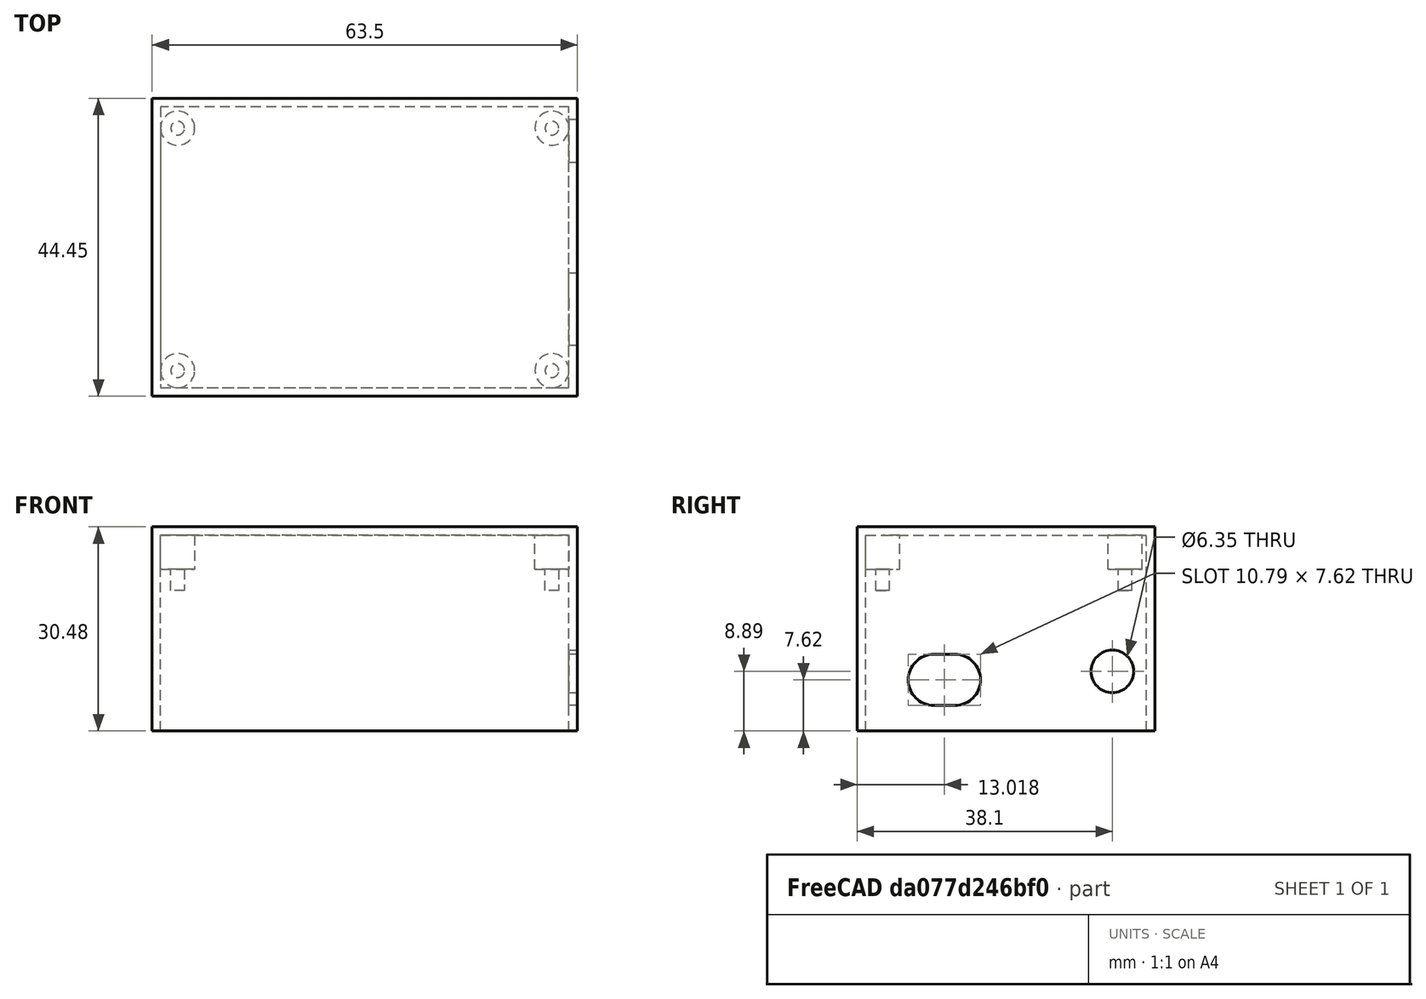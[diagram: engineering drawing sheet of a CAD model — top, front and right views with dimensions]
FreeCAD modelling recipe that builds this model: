
FCSTD DOCUMENT  (FreeCAD 0.18R4 (GitTag))
Label: BluetoothLightControlBox
License: All rights reserved
LicenseURL: http://en.wikipedia.org/wiki/All_rights_reserved
objects: Sketcher::SketchObject×5, PartDesign::Pad×3, PartDesign::Pocket×2, PartDesign::Body×1
note: 16 computed .brp shape members not serialized (recipe doc carries the construction recipe); baked Part::Feature solids carry a one-line shape summary decoded from their .brp

FEATURE [Sketcher::SketchObject] Sketch
  MapMode = 5
  Support = -> [XY_Plane]
  sketch-geometry (4):
    g0: LineSegment StartX=0 StartY=0 StartZ=0 EndX=63.5 EndY=0 EndZ=0
    g1: LineSegment StartX=63.5 StartY=0 StartZ=0 EndX=63.5 EndY=44.45 EndZ=0
    g2: LineSegment StartX=63.5 StartY=44.45 StartZ=0 EndX=0 EndY=44.45 EndZ=0
    g3: LineSegment StartX=0 StartY=44.45 StartZ=0 EndX=0 EndY=0 EndZ=0
  constraints (11):
    c: Coincident(g0,g1)
    c: Coincident(g1,g2)
    c: Coincident(g2,g3)
    c: Coincident(g3,g0)
    c: Horizontal(g0)
    c: Horizontal(g2)
    c: Vertical(g1)
    c: Vertical(g3)
    c: Coincident(g0,g-1)
    c: DistanceX(g2,g2) = 63.5
    c: DistanceY(g1,g1) = 44.45
FEATURE [PartDesign::Pad] Pad
  Length = 30.48
  Length2 = 100.076
  Profile = -> Sketch
  Type = 0
FEATURE [Sketcher::SketchObject] Sketch001
  MapMode = 5
  Placement = pos=(0,0,0) rot=(1,0,0;3.14159rad)
  Support = -> [Pad]
  sketch-geometry (4):
    g0: LineSegment StartX=1.27 StartY=-1.27 StartZ=0 EndX=62.23 EndY=-1.27 EndZ=0
    g1: LineSegment StartX=62.23 StartY=-1.27 StartZ=0 EndX=62.23 EndY=-43.18 EndZ=0
    g2: LineSegment StartX=62.23 StartY=-43.18 StartZ=0 EndX=1.27 EndY=-43.18 EndZ=0
    g3: LineSegment StartX=1.27 StartY=-43.18 StartZ=0 EndX=1.27 EndY=-1.27 EndZ=0
  constraints (12):
    c: Coincident(g0,g1)
    c: Coincident(g1,g2)
    c: Coincident(g2,g3)
    c: Coincident(g3,g0)
    c: Horizontal(g0)
    c: Horizontal(g2)
    c: Vertical(g1)
    c: Vertical(g3)
    c: DistanceY(g1,g1) = 41.91
    c: DistanceX(g0,g0) = 60.96
    c: DistanceX(g-1,g0) = 1.27
    c: DistanceY(g0,g-1) = 1.27
FEATURE [PartDesign::Pocket] Pocket
  BaseFeature = -> Pad
  Length = 29.21
  Length2 = 100.076
  Profile = -> Sketch001
  Type = 0
FEATURE [Sketcher::SketchObject] Sketch002
  MapMode = 5
  Placement = pos=(0,0,29.21) rot=(1,0,0;3.14159rad)
  Support = -> [Pocket]
  sketch-geometry (8):
    g0: Circle CenterX=3.81 CenterY=-40.005 CenterZ=0 NormalX=0 NormalY=0 NormalZ=1 AngleXU=0 Radius=2.54
    g1: Circle CenterX=59.69 CenterY=-40.005 CenterZ=0 NormalX=0 NormalY=0 NormalZ=1 AngleXU=0 Radius=2.54
    g2: Circle CenterX=3.81 CenterY=-3.81 CenterZ=0 NormalX=0 NormalY=0 NormalZ=1 AngleXU=0 Radius=2.54
    g3: Circle CenterX=59.69 CenterY=-3.81 CenterZ=0 NormalX=0 NormalY=0 NormalZ=1 AngleXU=0 Radius=2.54
    g4: LineSegment [constr] StartX=3.81 StartY=-3.81 StartZ=0 EndX=59.69 EndY=-3.81 EndZ=0
    g5: LineSegment [constr] StartX=59.69 StartY=-3.81 StartZ=0 EndX=59.69 EndY=-40.005 EndZ=0
    g6: LineSegment [constr] StartX=59.69 StartY=-40.005 StartZ=0 EndX=3.81 EndY=-40.005 EndZ=0
    g7: LineSegment [constr] StartX=3.81 StartY=-40.005 StartZ=0 EndX=3.81 EndY=-3.81 EndZ=0
  constraints (20):
    c: Coincident(g4,g5)
    c: Coincident(g5,g6)
    c: Coincident(g6,g7)
    c: Coincident(g7,g4)
    c: Horizontal(g4)
    c: Horizontal(g6)
    c: Vertical(g5)
    c: Vertical(g7)
    c: DistanceY(g5,g5) = 36.195
    c: DistanceX(g4,g4) = 55.88
    c: DistanceX(g-1,g4) = 3.81
    c: DistanceY(g4,g-1) = 3.81
    c: Radius(g2) = 2.54
    c: Equal(g2,g3)
    c: Equal(g2,g1)
    c: Equal(g2,g0)
    c: Coincident(g2,g4)
    c: Coincident(g3,g4)
    c: Coincident(g1,g5)
    c: Coincident(g0,g6)
FEATURE [PartDesign::Pad] Pad001
  BaseFeature = -> Pocket
  Length = 5.08
  Length2 = 100.076
  Profile = -> Sketch002
  Type = 0
FEATURE [Sketcher::SketchObject] Sketch003
  MapMode = 5
  Placement = pos=(63.5,0,0) rot=(0.57735,0.57735,0.57735;2.0944rad)
  Support = -> [Pad001]
  sketch-geometry (5):
    g0: ArcOfCircle CenterX=11.43 CenterY=7.62 CenterZ=0 NormalX=0 NormalY=0 NormalZ=1 AngleXU=0 Radius=3.81 StartAngle=1.5708 EndAngle=4.71239
    g1: ArcOfCircle CenterX=14.605 CenterY=7.62 CenterZ=0 NormalX=0 NormalY=0 NormalZ=1 AngleXU=0 Radius=3.81 StartAngle=4.71239 EndAngle=7.85398
    g2: LineSegment StartX=11.43 StartY=3.81 StartZ=0 EndX=14.605 EndY=3.81 EndZ=0
    g3: LineSegment StartX=11.43 StartY=11.43 StartZ=0 EndX=14.605 EndY=11.43 EndZ=0
    g4: Circle CenterX=38.1 CenterY=8.89 CenterZ=0 NormalX=0 NormalY=0 NormalZ=1 AngleXU=0 Radius=3.175
  constraints (13):
    c: Tangent(g0,g3) = 1.5708
    c: Tangent(g0,g2) = -1.5708
    c: Tangent(g2,g1) = -1.5708
    c: Tangent(g3,g1) = 1.5708
    c: Horizontal(g2)
    c: Equal(g0,g1)
    c: Radius(g1) = 3.81
    c: DistanceX(g3,g3) = 3.175
    c: DistanceY(g-1,g0) = 3.81
    c: DistanceX(g-1,g0) = 11.43
    c: Radius(g4) = 3.175
    c: DistanceX(g-1,g4) = 38.1
    c: DistanceY(g-1,g4) = 8.89
FEATURE [PartDesign::Pocket] Pocket001
  BaseFeature = -> Pad001
  Length = 5
  Length2 = 100.076
  Profile = -> Sketch003
  Type = 0
FEATURE [Sketcher::SketchObject] CopySketch004
  Placement = pos=(0,0,24.13) rot=(1,0,0;3.14159rad)
  sketch-geometry (8):
    g0: LineSegment [constr] StartX=3.81 StartY=-3.81 StartZ=0 EndX=59.69 EndY=-3.81 EndZ=0
    g1: LineSegment [constr] StartX=59.69 StartY=-3.81 StartZ=0 EndX=59.69 EndY=-40.005 EndZ=0
    g2: LineSegment [constr] StartX=59.69 StartY=-40.005 StartZ=0 EndX=3.81 EndY=-40.005 EndZ=0
    g3: LineSegment [constr] StartX=3.81 StartY=-40.005 StartZ=0 EndX=3.81 EndY=-3.81 EndZ=0
    g4: Circle CenterX=3.81 CenterY=-40.005 CenterZ=0 NormalX=0 NormalY=0 NormalZ=1 AngleXU=0 Radius=1.016
    g5: Circle CenterX=3.81 CenterY=-3.81 CenterZ=0 NormalX=0 NormalY=0 NormalZ=1 AngleXU=0 Radius=1.016
    g6: Circle CenterX=59.69 CenterY=-3.81 CenterZ=0 NormalX=0 NormalY=0 NormalZ=1 AngleXU=0 Radius=1.016
    g7: Circle CenterX=59.69 CenterY=-40.005 CenterZ=0 NormalX=0 NormalY=0 NormalZ=1 AngleXU=0 Radius=1.016
  constraints (16):
    c: Coincident(g0,g1)
    c: Coincident(g1,g2)
    c: Coincident(g2,g3)
    c: Coincident(g3,g0)
    c: Horizontal(g0)
    c: Horizontal(g2)
    c: Vertical(g1)
    c: Vertical(g3)
    c: DistanceY(g1,g1) = 36.195
    c: DistanceX(g0,g0) = 55.88
    c: DistanceX(g-1,g0) = 3.81
    c: DistanceY(g0,g-1) = 3.81
    c: Radius(g5) = 1.016
    c: Equal(g5,g6)
    c: Equal(g5,g7)
    c: Equal(g5,g4)
FEATURE [PartDesign::Pad] Pad002
  BaseFeature = -> Pocket001
  Length = 3.175
  Length2 = 100.076
  Profile = -> CopySketch004
  Type = 0
FEATURE [PartDesign::Body] Body
  Group = -> [Sketch,Pad,Sketch001,Pocket,Sketch002,Pad001,Sketch003,Pocket001,Pad002]
  Origin = -> Origin
  Tip = -> Pad002
